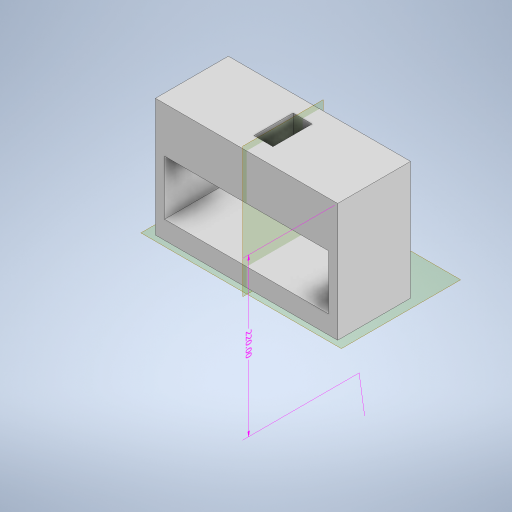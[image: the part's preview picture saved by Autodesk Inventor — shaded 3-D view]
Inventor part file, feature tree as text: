
AUTODESK INVENTOR PART (.ipt)
format: ipt  version: 2023 (Build 270158000, 158)  size: 314,368 bytes
history: native  units: mm
features: extrude x6, sketch x6, other x5, plane x4, split x1
ambient origin geometry x8: Origin, YZ Plane, XZ Plane, XY Plane, X Axis, Y Axis, Z Axis, Center Point
bodies: Body1 (feature_tree), Body2 (feature_tree)
feature tree (22):
  other  "Sólido1"
  other  "Anotaciones"
  extrude  "Extrusión1"  Depth=80.0mm
  extrude  "Extrusión2"  Depth=180.0mm
  extrude  "Extrusión3"  Depth=20.0mm
  extrude  "Extrusión4"  Depth=21.0mm
  plane  "Plano de trabajo1"
  extrude  "Extrusión6"  Depth=20.0mm
  plane  "Plano de trabajo3"
  extrude  "Extrusión7"  [1 undecoded]
  plane  "Plano de trabajo4"
  split  "Dividir1"
  other  "Suprimir cara4"
  plane  "Plano de trabajo5"
  sketch  "Boceto1"  dims[d0=200.0mm d1=80.0mm]
  sketch  "Boceto2"  dims[d2=130.0mm d3=0.0mm d4=180.0mm]
  sketch  "Boceto3"  dims[d5=60.0mm d6=20.0mm]
  sketch  "Boceto4"  dims[d7=60.0mm d8=0.0mm d9=21.0mm d10=43.0mm]
  sketch  "Boceto7"  dims[d11=43.0mm d12=0.0mm d13=20.0mm]
  other  "Sólido3"
  sketch  "Boceto10"  dims[d14=90.0mm d15=0.0mm d16=-90.0mm d28=20.0mm d29=20.0mm d30=30.0mm d31=30.0mm d32=20.0mm d33=35.0mm d34=35.0mm d35=69.0mm d36=10.0mm d37=0.0mm d45=1.5mm d50=10.0mm d51=0.0mm d52=10.0mm d53=89.5mm d54=90.0deg d38=3.166395mm d39=4.283575mm d40=220.0mm]
  other  "Cota lineal 1"
note: 1 required parameter value undecoded (feature->parameter linkage not recoverable at this tier; creation-order binding heuristic only, values carry confidence <= 0.55)
